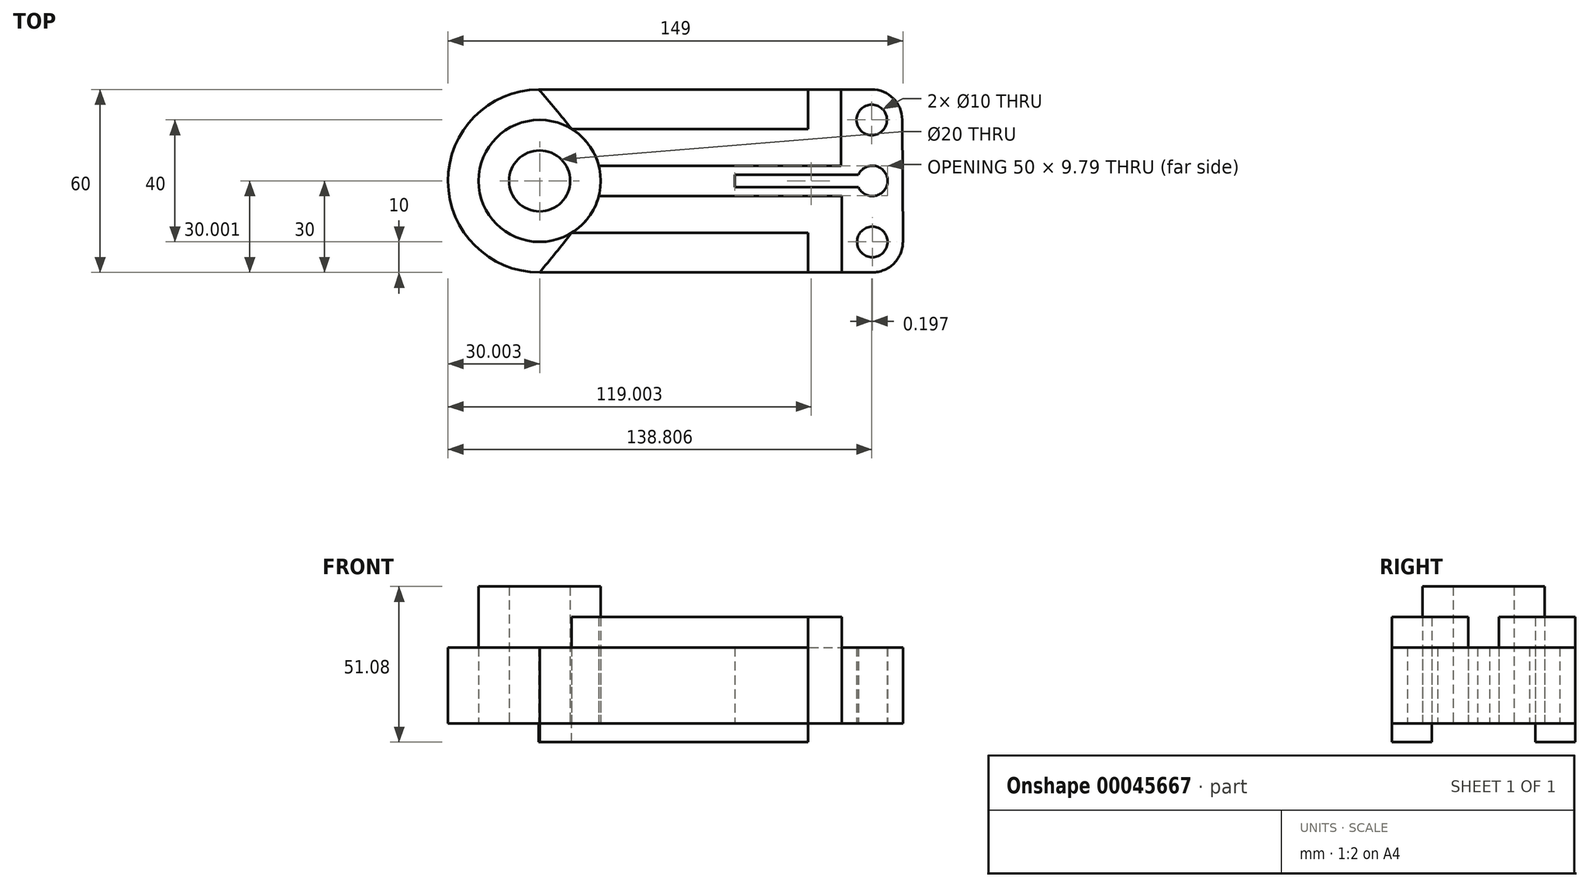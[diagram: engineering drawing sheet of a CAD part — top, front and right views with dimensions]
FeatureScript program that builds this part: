
annotation { "Feature Type Name" : "Feature", "Feature Type Description" : "" }
export const myFeature = defineFeature(function(context is Context, id is Id, definition is map)
    precondition{}
    {
        {
            var Q0;
            Q0=qCreatedBy(makeId("Top.planeOp"),FACE);
            var sketch = newSketch(context, id + "F0", { "sketchPlane" : qUnion([Q0])});
            skLineSegment(sketch, "E0.rect.bottom", {"start": v(-59.67, 30) * mm, "end": v(49.43, 30) * mm});
            skLineSegment(sketch, "E0.rect.top", {"start": v(-59.38, -30) * mm, "end": v(49.62, -30) * mm});
            skLineSegment(sketch, "E0.rect.right", {"start": v(59.43, 20.05) * mm, "end": v(59.62, -19.95) * mm});
            skArc(sketch, "E1", {"start": v(-59.67, 30) * mm, "mid": v(-89.38, -0.15) * mm, "end": v(-59.38, -30) * mm});
            skPoint(sketch, "E2.visualSharp", {"position": v(59.38, 30) * mm});
            skArc(sketch, "E2.filletArc", {"start": v(59.43, 20.05) * mm, "mid": v(56.48, 27.09) * mm, "end": v(49.43, 30) * mm});
            skPoint(sketch, "E3.visualSharp", {"position": v(59.67, -30) * mm});
            skArc(sketch, "E3.filletArc", {"start": v(49.62, -30) * mm, "mid": v(56.71, -27.05) * mm, "end": v(59.62, -19.95) * mm});
            skCircle(sketch, "E4", {"center": v(49.62, -20) * mm, "radius": 5 * mm});
            skCircle(sketch, "E5", {"center": v(49.43, 20) * mm, "radius": 5 * mm});
            skArc(sketch, "E6", {"start": v(45.04, -2) * mm, "mid": v(54.62, 0) * mm, "end": v(45.04, 2) * mm});
            skLineSegment(sketch, "E7", {"start": v(45.04, 2) * mm, "end": v(4.62, 2) * mm});
            skLineSegment(sketch, "E8", {"start": v(45.04, -2) * mm, "end": v(4.62, -2) * mm});
            skLineSegment(sketch, "E9", {"start": v(4.62, -2) * mm, "end": v(4.62, 2) * mm});
            skCircle(sketch, "E10", {"center": v(-59.38, 0) * mm, "radius": 20 * mm});
            skCircle(sketch, "E11", {"center": v(-59.38, 0) * mm, "radius": 10 * mm});
            skLineSegment(sketch, "E12", {"start": v(-29.43, -17) * mm, "end": v(-48.84, -17) * mm, "construction": true});
            skLineSegment(sketch, "E13", {"start": v(-29.43, 17) * mm, "end": v(-48.84, 17) * mm, "construction": true});
            skLineSegment(sketch, "E14", {"start": v(-48.84, 17) * mm, "end": v(28.62, 17) * mm});
            skLineSegment(sketch, "E15", {"start": v(-40.01, -5) * mm, "end": v(39.62, -5) * mm});
            skLineSegment(sketch, "E16", {"start": v(39.33, 5) * mm, "end": v(39.33, 30) * mm});
            skLineSegment(sketch, "E17", {"start": v(28.62, 17) * mm, "end": v(28.62, 30) * mm});
            skLineSegment(sketch, "E18", {"start": v(-48.84, -17) * mm, "end": v(28.62, -17) * mm});
            skLineSegment(sketch, "E19", {"start": v(28.62, -17) * mm, "end": v(28.62, -30) * mm});
            skLineSegment(sketch, "E20", {"start": v(39.62, -5) * mm, "end": v(39.62, -30) * mm});
            skLineSegment(sketch, "E21.trimOffspring", {"start": v(-40.01, 5) * mm, "end": v(39.33, 5) * mm});
            skArc(sketch, "E22", {"start": v(-59.38, -30) * mm, "mid": v(-54.05, -23.55) * mm, "end": v(-48.84, -17) * mm});
            skArc(sketch, "E23", {"start": v(-48.84, 17) * mm, "mid": v(-54.17, 23.57) * mm, "end": v(-59.67, 30) * mm});
            skSolve(sketch);
        }
        {
            var Q0;
            {var subQ4=sQuery(id+"F0.wireOp",EDGE,"E1");Q0=makeQuery(id+"F0.imprint","IMPRINT",FACE,{"disambiguationData":[TD([[makeQuery(id+"F0.imprint","IMPRINT",EDGE,{"derivedFrom":subQ4}),1.0]])]});}
            extrude(context, id + "F1", {"entities" : qUnion([Q0]), "depth" : 25 * mm});
        }
        {
            var Q0;
            Q0=makeQuery(id+"F0.imprint","IMPRINT",FACE,{"disambiguationData":[TD([[makeQuery(id+"F0.imprint","IMPRINT",EDGE,{"derivedFrom":sQuery(id+"F0.wireOp",EDGE,"E0.rect.right")}),-1.0]])]});
            extrude(context, id + "F2", {"entities" : qUnion([Q0]), "depth" : 25 * mm});
        }
        {
            var Q0;
            {var subQ3=sQuery(id+"F0.wireOp",EDGE,"E14");Q0=makeQuery(id+"F0.imprint","IMPRINT",FACE,{"disambiguationData":[TD([[makeQuery(id+"F0.imprint","IMPRINT",EDGE,{"derivedFrom":subQ3}),-1.0]])]});}
            var Q1;
            {var subQ3=sQuery(id+"F0.wireOp",EDGE,"E15");Q1=makeQuery(id+"F0.imprint","IMPRINT",FACE,{"disambiguationData":[TD([[makeQuery(id+"F0.imprint","IMPRINT",EDGE,{"derivedFrom":subQ3}),-1.0]])]});}
            extrude(context, id + "F3", {"entities" : qUnion([Q0, Q1]), "depth" : 35 * mm});
        }
        {
            var Q0;
            Q0=makeQuery(id+"F0.imprint","IMPRINT",FACE,{"disambiguationData":[TD([[makeQuery(id+"F0.imprint","IMPRINT",EDGE,{"derivedFrom":sQuery(id+"F0.wireOp",EDGE,"E11")}),-1.0]])]});
            extrude(context, id + "F4", {"entities" : qUnion([Q0]), "depth" : 45 * mm});
        }
        {
            var Q0;
            Q0=makeQuery(id+"F0.imprint","IMPRINT",FACE,{"disambiguationData":[TD([[makeQuery(id+"F0.imprint","IMPRINT",EDGE,{"derivedFrom":sQuery(id+"F0.wireOp",EDGE,"E14")}),1.0]])]});
            var Q1;
            Q1=makeQuery(id+"F0.imprint","IMPRINT",FACE,{"disambiguationData":[TD([[makeQuery(id+"F0.imprint","IMPRINT",EDGE,{"derivedFrom":sQuery(id+"F0.wireOp",EDGE,"E18")}),-1.0]])]});
            extrude(context, id + "F5", {"entities" : qUnion([Q0, Q1]), "oppositeDirection" : true, "depth" : 6.08 * mm});
        }
        {
            var Q0;
            Q0=makeQuery(id+"F5.opExtrude","CAP_FACE",FACE,{"disambiguationData":[OSD([sQuery(id+"F0.wireOp",EDGE,"E0.rect.bottom"),sQuery(id+"F0.wireOp",EDGE,"E14"),sQuery(id+"F0.wireOp",EDGE,"E17"),sQuery(id+"F0.wireOp",EDGE,"E23")])],"isStart":true});
            var Q1;
            Q1=makeQuery(id+"F5.opExtrude","CAP_FACE",FACE,{"disambiguationData":[OSD([sQuery(id+"F0.wireOp",EDGE,"E0.rect.top"),sQuery(id+"F0.wireOp",EDGE,"E18"),sQuery(id+"F0.wireOp",EDGE,"E19"),sQuery(id+"F0.wireOp",EDGE,"E22")])],"isStart":true});
            extrude(context, id + "F6", {"entities" : qUnion([Q0, Q1]), "depth" : 25 * mm});
        }
    });
